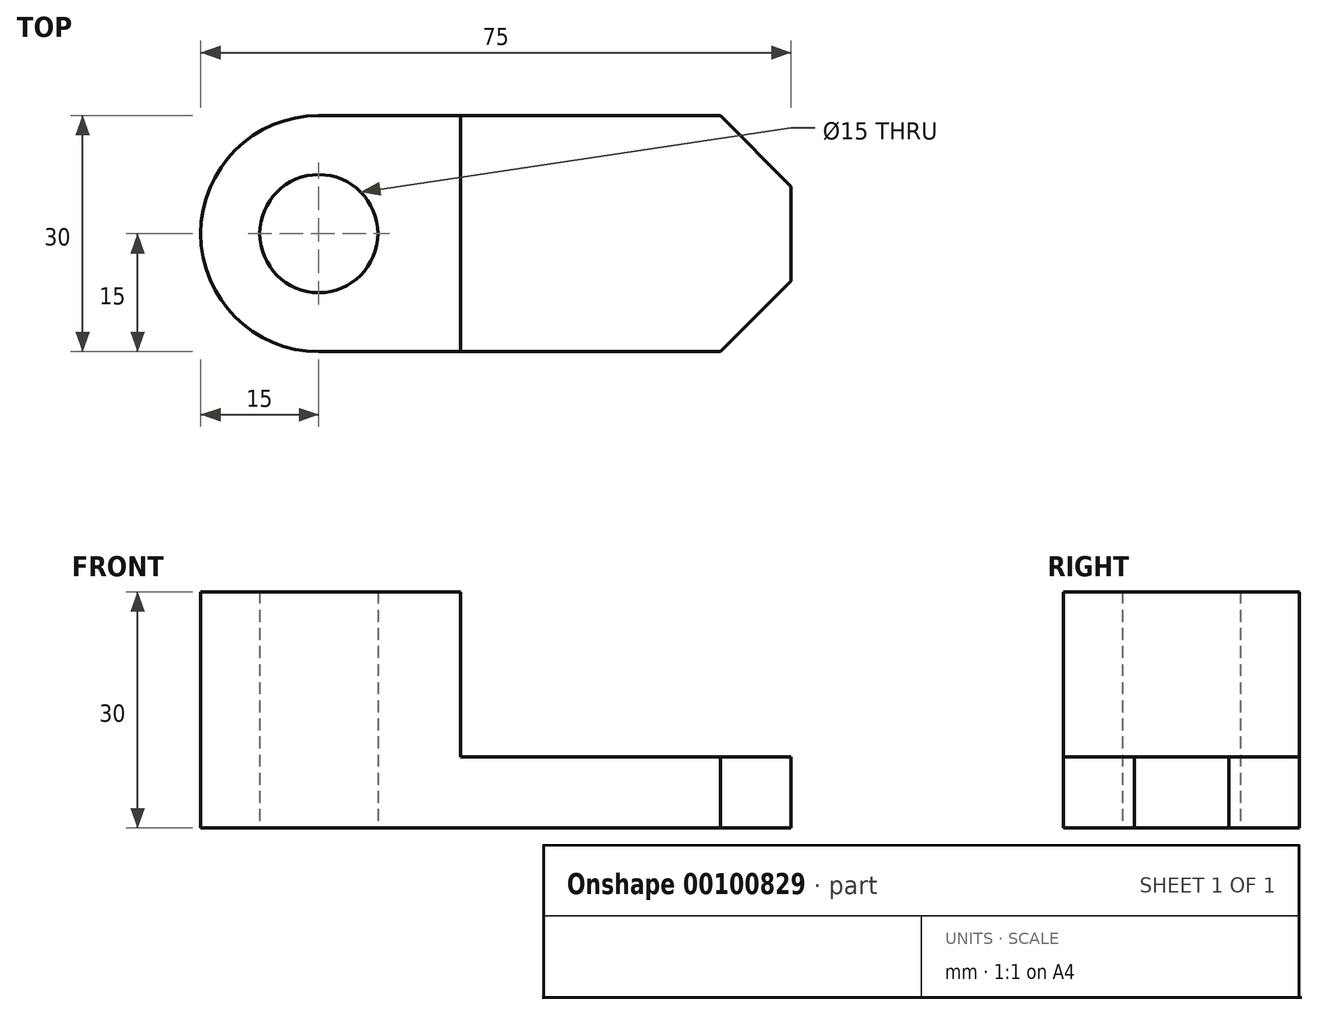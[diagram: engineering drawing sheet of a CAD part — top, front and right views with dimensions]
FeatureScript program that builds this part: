
annotation { "Feature Type Name" : "Feature", "Feature Type Description" : "" }
export const myFeature = defineFeature(function(context is Context, id is Id, definition is map)
    precondition{}
    {
        {
            var Q0;
            Q0=qCreatedBy(makeId("Top.planeOp"),FACE);
            var sketch = newSketch(context, id + "F0", { "sketchPlane" : qUnion([Q0])});
            skLineSegment(sketch, "E0.bottom", {"start": v(0, 0) * mm, "end": v(51, 0) * mm});
            skLineSegment(sketch, "E0.top", {"start": v(0, 30) * mm, "end": v(51, 30) * mm});
            skLineSegment(sketch, "E0.right", {"start": v(60, 9) * mm, "end": v(60, 21) * mm});
            skLineSegment(sketch, "E1", {"start": v(51, 30) * mm, "end": v(60, 21) * mm});
            skLineSegment(sketch, "E2", {"start": v(60, 9) * mm, "end": v(51, 0) * mm});
            skArc(sketch, "E3", {"start": v(0, 30) * mm, "mid": v(-15, 15) * mm, "end": v(0, 0) * mm});
            skCircle(sketch, "E4", {"center": v(0, 15) * mm, "radius": 7.5 * mm});
            skSolve(sketch);
        }
        {
            var Q0;
            Q0=makeQuery(id+"F0.imprint","IMPRINT",FACE,{"disambiguationData":[TD([[makeQuery(id+"F0.imprint","IMPRINT",EDGE,{"derivedFrom":sQuery(id+"F0.wireOp",EDGE,"E0.bottom")}),1.0]])]});
            extrude(context, id + "F1", {"entities" : qUnion([Q0]), "depth" : 9 * mm});
        }
        {
            var Q0;
            Q0=makeQuery(id+"F1.opExtrude","CAP_FACE",FACE,{"disambiguationData":[OSD([sQuery(id+"F0.wireOp",EDGE,"E0.bottom"),sQuery(id+"F0.wireOp",EDGE,"E0.top"),sQuery(id+"F0.wireOp",EDGE,"E0.right"),sQuery(id+"F0.wireOp",EDGE,"E1"),sQuery(id+"F0.wireOp",EDGE,"E2"),sQuery(id+"F0.wireOp",EDGE,"E3"),sQuery(id+"F0.wireOp",EDGE,"E4")])],"isStart":false});
            var sketch = newSketch(context, id + "F2", { "sketchPlane" : qUnion([Q0])});
            skLineSegment(sketch, "E5", {"start": v(18, 30) * mm, "end": v(18, 0) * mm});
            skSolve(sketch);
        }
        {
            var Q0;
            {var subQ2=sQuery(id+"F2.wireOp",EDGE,"E5");Q0=makeQuery(id+"F2.imprint","IMPRINT",FACE,{"disambiguationData":[TD([[makeQuery(id+"F2.imprint","IMPRINT",EDGE,{"derivedFrom":subQ2}),-1.0]])]});}
            extrude(context, id + "F3", {"entities" : qUnion([Q0]), "operationType" : NewBodyOperationType.ADD, "depth" : 21 * mm});
        }
        {
            var Q0;
            Q0=qCreatedBy(makeId("Front.planeOp"),FACE);
            cPlane(context, id + "F4", {"entities" : qUnion([Q0]), "cplaneType" : CPlaneType.OFFSET, "offset" : 15 * mm, "oppositeDirection" : true, "width" : 150 * mm, "height" : 150 * mm});
        }
    });
